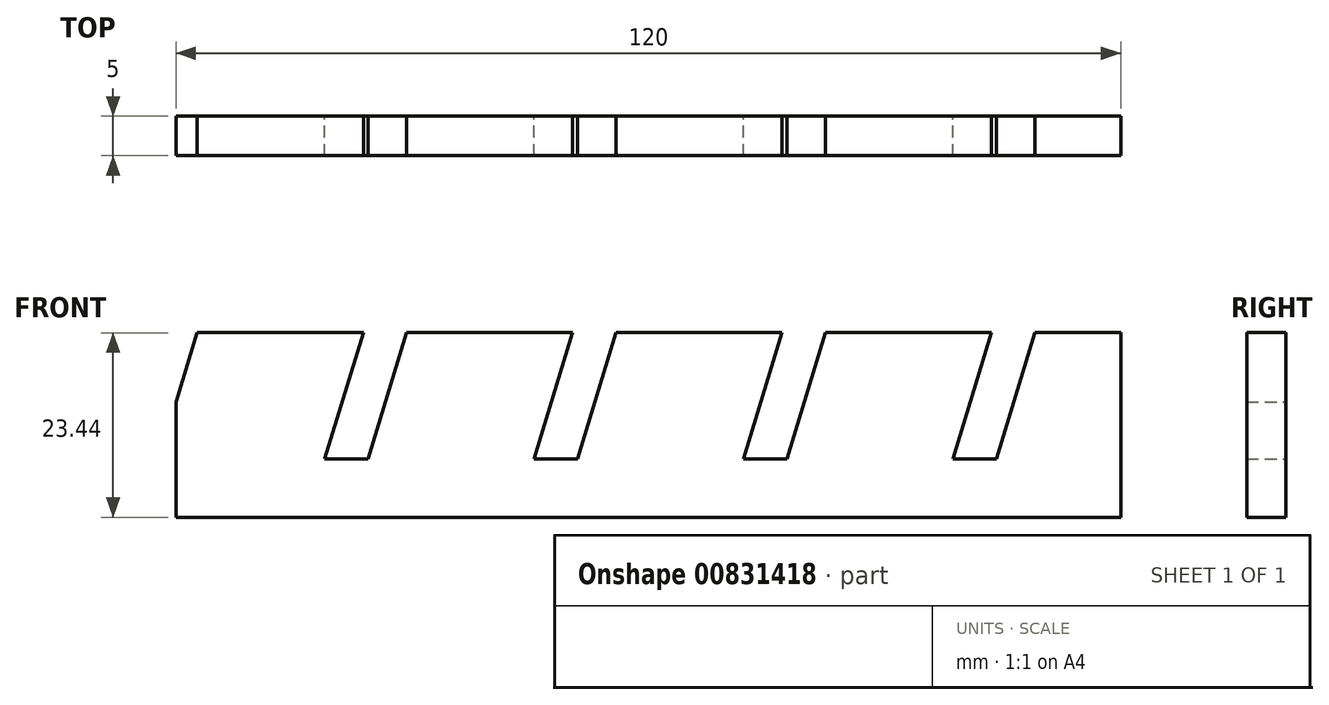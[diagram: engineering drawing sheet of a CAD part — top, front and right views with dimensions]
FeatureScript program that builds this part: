
annotation { "Feature Type Name" : "Feature", "Feature Type Description" : "" }
export const myFeature = defineFeature(function(context is Context, id is Id, definition is map)
    precondition{}
    {
        {
            var Q0;
            Q0=qCreatedBy(makeId("Front.planeOp"),FACE);
            var sketch = newSketch(context, id + "F0", { "sketchPlane" : qUnion([Q0])});
            skLineSegment(sketch, "E0.bottom", {"start": v(0, 0) * mm, "end": v(120, 0) * mm});
            skLineSegment(sketch, "E0.top", {"start": v(2.69, 23.44) * mm, "end": v(23.79, 23.44) * mm});
            skLineSegment(sketch, "E0.left", {"start": v(0, 0) * mm, "end": v(0, 14.64) * mm});
            skLineSegment(sketch, "E0.right", {"start": v(120, 0) * mm, "end": v(120, 23.44) * mm});
            skLineSegment(sketch, "E1", {"start": v(23.79, 23.44) * mm, "end": v(18.88, 7.38) * mm});
            skLineSegment(sketch, "E2", {"start": v(24.38, 7.38) * mm, "end": v(29.29, 23.44) * mm});
            skLineSegment(sketch, "E3", {"start": v(18.88, 7.38) * mm, "end": v(24.38, 7.38) * mm});
            skLineSegment(sketch, "E4.trimOffspring", {"start": v(29.29, 23.44) * mm, "end": v(50.39, 23.44) * mm});
            skLineSegment(sketch, "E5.1.0.0", {"start": v(50.98, 7.38) * mm, "end": v(55.89, 23.44) * mm});
            skLineSegment(sketch, "E5.1.0.1", {"start": v(45.48, 7.38) * mm, "end": v(50.98, 7.38) * mm});
            skLineSegment(sketch, "E5.1.0.2", {"start": v(50.39, 23.44) * mm, "end": v(45.48, 7.38) * mm});
            skLineSegment(sketch, "E5.2.0.0", {"start": v(77.58, 7.38) * mm, "end": v(82.49, 23.44) * mm});
            skLineSegment(sketch, "E5.2.0.1", {"start": v(72.08, 7.38) * mm, "end": v(77.58, 7.38) * mm});
            skLineSegment(sketch, "E5.2.0.2", {"start": v(76.99, 23.44) * mm, "end": v(72.08, 7.38) * mm});
            skLineSegment(sketch, "E5.3.0.0", {"start": v(104.18, 7.38) * mm, "end": v(109.09, 23.44) * mm});
            skLineSegment(sketch, "E5.3.0.1", {"start": v(98.68, 7.38) * mm, "end": v(104.18, 7.38) * mm});
            skLineSegment(sketch, "E5.3.0.2", {"start": v(103.59, 23.44) * mm, "end": v(98.68, 7.38) * mm});
            skLineSegment(sketch, "E5.direction1", {"start": v(24.38, 7.38) * mm, "end": v(50.98, 7.38) * mm, "construction": true});
            skLineSegment(sketch, "E6.trimOffspring", {"start": v(55.89, 23.44) * mm, "end": v(76.99, 23.44) * mm});
            skLineSegment(sketch, "E7.trimOffspring", {"start": v(82.49, 23.44) * mm, "end": v(103.59, 23.44) * mm});
            skLineSegment(sketch, "E8.trimOffspring", {"start": v(109.09, 23.44) * mm, "end": v(120, 23.44) * mm});
            skLineSegment(sketch, "E9.1.0.2", {"start": v(0, 14.64) * mm, "end": v(2.69, 23.44) * mm});
            skLineSegment(sketch, "E9.direction1", {"start": v(18.88, 7.38) * mm, "end": v(-2.22, 7.38) * mm, "construction": true});
            skSolve(sketch);
        }
        {
            var Q0;
            Q0=makeQuery(id+"F0.imprint","IMPRINT",FACE,{"disambiguationData":[TD([[makeQuery(id+"F0.imprint","IMPRINT",EDGE,{"derivedFrom":sQuery(id+"F0.wireOp",EDGE,"E0.bottom")}),1.0]])]});
            extrude(context, id + "F1", {"entities" : qUnion([Q0]), "depth" : 5 * mm, "offsetDistance" : 25 * mm});
        }
    });
